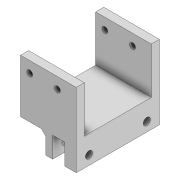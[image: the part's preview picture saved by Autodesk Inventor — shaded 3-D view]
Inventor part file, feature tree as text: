
AUTODESK INVENTOR PART (.ipt)
format: ipt  version: 2022 (Build 260153000, 153)  size: 208,384 bytes
history: native  units: mm
features: extrude x5, thicken_offset x5, sketch x5, chamfer x1, projected_geometry x1
ambient origin geometry x8: Origin, YZ Plane, XZ Plane, XY Plane, X Axis, Y Axis, Z Axis, Center Point
bodies: Solid1 (feature_tree)
feature tree (17):
  extrude  "Extrusion1"  Depth=29.0mm
  extrude  "Extrusion2"  Depth=2.5mm
  extrude  "Extrusion4"  Depth=8.0mm
  extrude  "Extrusion5"  Depth=5.0mm
  extrude  "Extrusion6"  Depth=5.0mm
  thicken_offset  "Thicken1"
  thicken_offset  "Thicken2"
  chamfer  "Chamfer1"  Distance=12.0mm
  thicken_offset  "Thicken3"
  thicken_offset  "Thicken4"
  thicken_offset  "Thicken5"
  sketch  "Sketch1"  dims[d0=29.0mm d1=14.5mm]
  sketch  "Sketch2"  dims[d3=2.5mm d4=2.5mm]
  sketch  "Sketch5"  dims[d5=16.0mm d6=8.0mm]
  sketch  "Sketch6"  dims[d7=5.0mm d8=5.0mm]
  sketch  "Sketch8"  dims[d9=2.5mm d10=2.5mm d11=12.0mm d12=12.0mm d13=5.0mm d14=3.0mm d15=0.0mm d17=3.0mm d18=9.0mm d19=0.0mm d24=3.0mm d25=3.0mm d26=3.0mm d27=3.0mm d30=20.0mm d31=0.0mm d34=2.5mm d38=50.0mm d39=0.0mm d40=3.0mm d41=5.0mm d42=3.1mm d43=3.1mm d46=4.0mm d47=4.0mm d48=100.0mm d49=0.0mm d50=0.0mm d53=2.5mm d54=4.0mm d55=6.0mm d56=15.25mm d57=15.25mm d58=0.1mm d59=0.1mm d60=0.1mm d61=0.1mm d62=2.0mm d63=2.0mm d64=45.0deg d65=5.0mm d66=5.0mm d67=2.1mm d68=2.1mm d69=0.5mm d70=0.5mm d71=0.5mm d72=0.5mm]
  projected_geometry  "Projected Loop1"
